annotation { "Feature Type Name" : "Feature", "Feature Type Description" : "" }
export const myFeature = defineFeature(function(context is Context, id is Id, definition is map)
    precondition{}
    {
        {
            var Q0;
            Q0=qCreatedBy(makeId("Right.planeOp"),FACE);
            var sketch = newSketch(context, id + "F0", { "sketchPlane" : qUnion([Q0])});
            skLineSegment(sketch, "E0", {"start": v(-64.38, 0) * mm, "end": v(62.76, 0) * mm, "construction": true});
            skLineSegment(sketch, "E1", {"start": v(-28.58, 0) * mm, "end": v(28.58, 0) * mm});
            skLineSegment(sketch, "E2", {"start": v(-28.58, 0) * mm, "end": v(-28.58, 4.76) * mm});
            skLineSegment(sketch, "E3", {"start": v(0, 21.68) * mm, "end": v(0, -31.61) * mm, "construction": true});
            skPoint(sketch, "E4", {"position": v(0, -63.5) * mm});
            skArc(sketch, "E5", {"start": v(28.58, 4.76) * mm, "mid": v(0, 10.5) * mm, "end": v(-28.58, 4.76) * mm});
            skLineSegment(sketch, "E6", {"start": v(28.58, 0) * mm, "end": v(28.58, 4.76) * mm});
            skSolve(sketch);
        }
        {
            var Q0;
            Q0 = qSketchRegion(id + "F0", true);
            extrude(context, id + "F1", {"entities" : qUnion([Q0]), "endBound" : BoundingType.SYMMETRIC, "depth" : 152.4 * mm, "offsetDistance" : 25.4 * mm});
        }
        {
            var Q0;
            Q0=qCreatedBy(makeId("Right.planeOp"),FACE);
            var sketch = newSketch(context, id + "F2", { "sketchPlane" : qUnion([Q0])});
            skLineSegment(sketch, "E7.bottom", {"start": v(-22.22, 24.41) * mm, "end": v(22.23, 24.41) * mm});
            skLineSegment(sketch, "E7.left", {"start": v(-22.22, 24.41) * mm, "end": v(-22.22, 7) * mm});
            skLineSegment(sketch, "E7.right", {"start": v(22.23, 24.41) * mm, "end": v(22.23, 7) * mm});
            skLineSegment(sketch, "E8", {"start": v(0, 26.13) * mm, "end": v(0, -12.17) * mm, "construction": true});
            skLineSegment(sketch, "E9", {"start": v(-39.48, 0) * mm, "end": v(39.93, 0) * mm, "construction": true});
            skLineSegment(sketch, "E10", {"start": v(-3.17, 21.37) * mm, "end": v(-3.17, -2.67) * mm, "construction": true});
            skLineSegment(sketch, "E11", {"start": v(-6.35, 21.57) * mm, "end": v(-6.35, -2.87) * mm, "construction": true});
            skLineSegment(sketch, "E12", {"start": v(-9.52, 21.78) * mm, "end": v(-9.52, -3.08) * mm, "construction": true});
            skLineSegment(sketch, "E13", {"start": v(-12.7, 21.89) * mm, "end": v(-12.7, -4.22) * mm, "construction": true});
            skLineSegment(sketch, "E14", {"start": v(-15.88, 21.89) * mm, "end": v(-15.88, -4.43) * mm, "construction": true});
            skLineSegment(sketch, "E15", {"start": v(-19.05, 22.3) * mm, "end": v(-19.05, -4.9) * mm, "construction": true});
            skArc(sketch, "E16", {"start": v(-19.58, 5.95) * mm, "mid": v(-20.33, 6.32) * mm, "end": v(-21.17, 6.26) * mm});
            skArc(sketch, "E17", {"start": v(-16.4, 5.95) * mm, "mid": v(-17.46, 6.35) * mm, "end": v(-18.52, 5.95) * mm});
            skArc(sketch, "E18", {"start": v(-13.23, 5.95) * mm, "mid": v(-14.29, 6.35) * mm, "end": v(-15.35, 5.95) * mm});
            skArc(sketch, "E19", {"start": v(-10.05, 5.95) * mm, "mid": v(-11.11, 6.35) * mm, "end": v(-12.17, 5.95) * mm});
            skArc(sketch, "E20", {"start": v(-6.88, 5.95) * mm, "mid": v(-7.94, 6.35) * mm, "end": v(-9, 5.95) * mm});
            skArc(sketch, "E21", {"start": v(-3.7, 5.95) * mm, "mid": v(-4.76, 6.35) * mm, "end": v(-5.82, 5.95) * mm});
            skArc(sketch, "E22", {"start": v(-0.53, 5.95) * mm, "mid": v(-1.59, 6.35) * mm, "end": v(-2.65, 5.95) * mm});
            skArc(sketch, "E23.MirrorCS", {"start": v(19.58, 5.95) * mm, "mid": v(20.33, 6.32) * mm, "end": v(21.17, 6.26) * mm});
            skArc(sketch, "E24.MirrorCS", {"start": v(16.4, 5.95) * mm, "mid": v(17.46, 6.35) * mm, "end": v(18.52, 5.95) * mm});
            skArc(sketch, "E25.MirrorCS", {"start": v(6.88, 5.95) * mm, "mid": v(7.94, 6.35) * mm, "end": v(9, 5.95) * mm});
            skArc(sketch, "E26.MirrorCS", {"start": v(3.7, 5.95) * mm, "mid": v(4.76, 6.35) * mm, "end": v(5.82, 5.95) * mm});
            skArc(sketch, "E27.MirrorCS", {"start": v(10.05, 5.95) * mm, "mid": v(11.11, 6.35) * mm, "end": v(12.17, 5.95) * mm});
            skArc(sketch, "E28.MirrorCS", {"start": v(13.23, 5.95) * mm, "mid": v(14.29, 6.35) * mm, "end": v(15.35, 5.95) * mm});
            skArc(sketch, "E29.MirrorCS", {"start": v(0.53, 5.95) * mm, "mid": v(1.59, 6.35) * mm, "end": v(2.65, 5.95) * mm});
            skArc(sketch, "E30.filletArc", {"start": v(-19.58, 5.95) * mm, "mid": v(-19.05, 5.74) * mm, "end": v(-18.52, 5.95) * mm});
            skArc(sketch, "E31.filletArc", {"start": v(-22.22, 7) * mm, "mid": v(-21.89, 6.36) * mm, "end": v(-21.17, 6.26) * mm});
            skArc(sketch, "E32.filletArc", {"start": v(-16.4, 5.95) * mm, "mid": v(-15.88, 5.74) * mm, "end": v(-15.35, 5.95) * mm});
            skArc(sketch, "E33.filletArc", {"start": v(-13.23, 5.95) * mm, "mid": v(-12.7, 5.74) * mm, "end": v(-12.17, 5.95) * mm});
            skArc(sketch, "E34.filletArc", {"start": v(-10.05, 5.95) * mm, "mid": v(-9.52, 5.74) * mm, "end": v(-9, 5.95) * mm});
            skArc(sketch, "E35.filletArc", {"start": v(-6.88, 5.95) * mm, "mid": v(-6.35, 5.74) * mm, "end": v(-5.82, 5.95) * mm});
            skArc(sketch, "E36.filletArc", {"start": v(-3.7, 5.95) * mm, "mid": v(-3.17, 5.74) * mm, "end": v(-2.65, 5.95) * mm});
            skArc(sketch, "E37.filletArc", {"start": v(-0.53, 5.95) * mm, "mid": v(0, 5.74) * mm, "end": v(0.53, 5.95) * mm});
            skArc(sketch, "E38.filletArc", {"start": v(2.65, 5.95) * mm, "mid": v(3.17, 5.74) * mm, "end": v(3.7, 5.95) * mm});
            skArc(sketch, "E39.filletArc", {"start": v(5.82, 5.95) * mm, "mid": v(6.35, 5.74) * mm, "end": v(6.88, 5.95) * mm});
            skArc(sketch, "E40.filletArc", {"start": v(9, 5.95) * mm, "mid": v(9.52, 5.74) * mm, "end": v(10.05, 5.95) * mm});
            skArc(sketch, "E41.filletArc", {"start": v(12.17, 5.95) * mm, "mid": v(12.7, 5.74) * mm, "end": v(13.23, 5.95) * mm});
            skArc(sketch, "E42.filletArc", {"start": v(15.35, 5.95) * mm, "mid": v(15.88, 5.74) * mm, "end": v(16.4, 5.95) * mm});
            skArc(sketch, "E43.filletArc", {"start": v(18.52, 5.95) * mm, "mid": v(19.05, 5.74) * mm, "end": v(19.58, 5.95) * mm});
            skArc(sketch, "E44.filletArc", {"start": v(21.17, 6.26) * mm, "mid": v(21.89, 6.36) * mm, "end": v(22.23, 7) * mm});
            skSolve(sketch);
        }
        {
            var Q0;
            Q0 = qSketchRegion(id + "F2", true);
            extrude(context, id + "F3", {"entities" : qUnion([Q0]), "operationType" : NewBodyOperationType.REMOVE, "endBound" : BoundingType.SYMMETRIC, "depth" : 139.7 * mm, "offsetDistance" : 25.4 * mm});
        }
        {
            var Q0;
            Q0=qCreatedBy(makeId("Top.planeOp"),FACE);
            var sketch = newSketch(context, id + "F4", { "sketchPlane" : qUnion([Q0])});
            skLineSegment(sketch, "E45", {"start": v(-61.52, 0) * mm, "end": v(67.76, 0) * mm, "construction": true});
            skLineSegment(sketch, "E46", {"start": v(0, 23.15) * mm, "end": v(0, -30.49) * mm, "construction": true});
            skText(sketch, "E47", { "text": "Pappy Bar", "fontName": "RobotoSlab-Bold.ttf"});
            const initialGuessF4  = {"E47": [-0.0635, -0.00927, 1, 0, 0.01857]};
            skSetInitialGuess(sketch, initialGuessF4);
            skSolve(sketch);
        }
        {
            var Q0;
            Q0 = qSketchRegion(id + "F4", true);
            extrude(context, id + "F5", {"entities" : qUnion([Q0]), "operationType" : NewBodyOperationType.ADD, "depth" : 12.7 * mm, "offsetDistance" : 25.4 * mm});
        }
        {
            var Q0;
            Q0=qCreatedBy(makeId("Right.planeOp"),FACE);
            var sketch = newSketch(context, id + "F6", { "sketchPlane" : qUnion([Q0])});
            skLineSegment(sketch, "E48", {"start": v(0, 61.11) * mm, "end": v(0, -83.47) * mm, "construction": true});
            skLineSegment(sketch, "E49", {"start": v(-121.03, 0) * mm, "end": v(89.55, 0) * mm, "construction": true});
            skPoint(sketch, "E50", {"position": v(0, -65.09) * mm});
            skPoint(sketch, "E51", {"position": v(28.58, 3.18) * mm});
            skArc(sketch, "E52", {"start": v(19.05, 6.42) * mm, "mid": v(0, 8.91) * mm, "end": v(-19.05, 6.42) * mm});
            skLineSegment(sketch, "E53.bottom", {"start": v(-19.05, 51.23) * mm, "end": v(19.05, 51.23) * mm});
            skLineSegment(sketch, "E53.left", {"start": v(-19.05, 51.23) * mm, "end": v(-19.05, 6.42) * mm});
            skLineSegment(sketch, "E53.right", {"start": v(19.05, 51.23) * mm, "end": v(19.05, 6.42) * mm});
            skSolve(sketch);
        }
        {
            var Q0;
            Q0 = qSketchRegion(id + "F6", true);
            extrude(context, id + "F7", {"entities" : qUnion([Q0]), "operationType" : NewBodyOperationType.REMOVE, "endBound" : BoundingType.SYMMETRIC, "oppositeDirection" : true, "depth" : 130.17 * mm, "offsetDistance" : 25.4 * mm});
        }
        {
            var Q0;
            Q0=makeQuery(id+"F1.opExtrude","CAP_EDGE",EDGE,{"disambiguationData":[OSD([sQuery(id+"F0.wireOp",EDGE,"E2")])],"isStart":true});
            var Q1;
            Q1=makeQuery(id+"F1.opExtrude","CAP_EDGE",EDGE,{"disambiguationData":[OSD([sQuery(id+"F0.wireOp",EDGE,"E5")])],"isStart":true});
            var Q2;
            Q2=makeQuery(id+"F1.opExtrude","SWEPT_EDGE",EDGE,{"disambiguationData":[OSD([sQuery(id+"F0.wireOp",EDGE,"E2"),sQuery(id+"F0.wireOp",EDGE,"E5")])]});
            var Q3;
            Q3=makeQuery(id+"F1.opExtrude","CAP_EDGE",EDGE,{"disambiguationData":[OSD([sQuery(id+"F0.wireOp",EDGE,"E6")])],"isStart":true});
            var Q4;
            Q4=makeQuery(id+"F1.opExtrude","SWEPT_EDGE",EDGE,{"disambiguationData":[OSD([sQuery(id+"F0.wireOp",EDGE,"E5"),sQuery(id+"F0.wireOp",EDGE,"E6")])]});
            var Q5;
            Q5=makeQuery(id+"F1.opExtrude","CAP_EDGE",EDGE,{"disambiguationData":[OSD([sQuery(id+"F0.wireOp",EDGE,"E6")])],"isStart":false});
            var Q6;
            Q6=makeQuery(id+"F1.opExtrude","CAP_EDGE",EDGE,{"disambiguationData":[OSD([sQuery(id+"F0.wireOp",EDGE,"E5")])],"isStart":false});
            var Q7;
            Q7=makeQuery(id+"F1.opExtrude","CAP_EDGE",EDGE,{"disambiguationData":[OSD([sQuery(id+"F0.wireOp",EDGE,"E2")])],"isStart":false});
            var Q8;
            Q8=makeQuery(id+"F3.boolean.opBoolean","INTERSECT",EDGE,{"derivedFrom":[makeQuery(id+"F1.opExtrude","SWEPT_FACE",FACE,{"disambiguationData":[OSD([sQuery(id+"F0.wireOp",EDGE,"E5")])]}),makeQuery(id+"F3.opExtrude","CAP_FACE",FACE,{"disambiguationData":[OSD([sQuery(id+"F2.wireOp",EDGE,"E7.bottom"),sQuery(id+"F2.wireOp",EDGE,"E7.left"),sQuery(id+"F2.wireOp",EDGE,"E7.right"),sQuery(id+"F2.wireOp",EDGE,"E16"),sQuery(id+"F2.wireOp",EDGE,"E17"),sQuery(id+"F2.wireOp",EDGE,"E18"),sQuery(id+"F2.wireOp",EDGE,"E19"),sQuery(id+"F2.wireOp",EDGE,"E20"),sQuery(id+"F2.wireOp",EDGE,"E21"),sQuery(id+"F2.wireOp",EDGE,"E22"),sQuery(id+"F2.wireOp",EDGE,"E23.MirrorCS"),sQuery(id+"F2.wireOp",EDGE,"E24.MirrorCS"),sQuery(id+"F2.wireOp",EDGE,"E25.MirrorCS"),sQuery(id+"F2.wireOp",EDGE,"E26.MirrorCS"),sQuery(id+"F2.wireOp",EDGE,"E27.MirrorCS"),sQuery(id+"F2.wireOp",EDGE,"E28.MirrorCS"),sQuery(id+"F2.wireOp",EDGE,"E29.MirrorCS"),sQuery(id+"F2.wireOp",EDGE,"E30.filletArc"),sQuery(id+"F2.wireOp",EDGE,"E31.filletArc"),sQuery(id+"F2.wireOp",EDGE,"E32.filletArc"),sQuery(id+"F2.wireOp",EDGE,"E33.filletArc"),sQuery(id+"F2.wireOp",EDGE,"E34.filletArc"),sQuery(id+"F2.wireOp",EDGE,"E35.filletArc"),sQuery(id+"F2.wireOp",EDGE,"E36.filletArc"),sQuery(id+"F2.wireOp",EDGE,"E37.filletArc"),sQuery(id+"F2.wireOp",EDGE,"E38.filletArc"),sQuery(id+"F2.wireOp",EDGE,"E39.filletArc"),sQuery(id+"F2.wireOp",EDGE,"E40.filletArc"),sQuery(id+"F2.wireOp",EDGE,"E41.filletArc"),sQuery(id+"F2.wireOp",EDGE,"E42.filletArc"),sQuery(id+"F2.wireOp",EDGE,"E43.filletArc"),sQuery(id+"F2.wireOp",EDGE,"E44.filletArc")])],"isStart":true})]});
            var Q9;
            Q9=makeQuery(id+"F3.boolean.opBoolean","INTERSECT",EDGE,{"derivedFrom":[makeQuery(id+"F1.opExtrude","SWEPT_FACE",FACE,{"disambiguationData":[OSD([sQuery(id+"F0.wireOp",EDGE,"E5")])]}),makeQuery(id+"F3.opExtrude","CAP_FACE",FACE,{"disambiguationData":[OSD([sQuery(id+"F2.wireOp",EDGE,"E7.bottom"),sQuery(id+"F2.wireOp",EDGE,"E7.left"),sQuery(id+"F2.wireOp",EDGE,"E7.right"),sQuery(id+"F2.wireOp",EDGE,"E16"),sQuery(id+"F2.wireOp",EDGE,"E17"),sQuery(id+"F2.wireOp",EDGE,"E18"),sQuery(id+"F2.wireOp",EDGE,"E19"),sQuery(id+"F2.wireOp",EDGE,"E20"),sQuery(id+"F2.wireOp",EDGE,"E21"),sQuery(id+"F2.wireOp",EDGE,"E22"),sQuery(id+"F2.wireOp",EDGE,"E23.MirrorCS"),sQuery(id+"F2.wireOp",EDGE,"E24.MirrorCS"),sQuery(id+"F2.wireOp",EDGE,"E25.MirrorCS"),sQuery(id+"F2.wireOp",EDGE,"E26.MirrorCS"),sQuery(id+"F2.wireOp",EDGE,"E27.MirrorCS"),sQuery(id+"F2.wireOp",EDGE,"E28.MirrorCS"),sQuery(id+"F2.wireOp",EDGE,"E29.MirrorCS"),sQuery(id+"F2.wireOp",EDGE,"E30.filletArc"),sQuery(id+"F2.wireOp",EDGE,"E31.filletArc"),sQuery(id+"F2.wireOp",EDGE,"E32.filletArc"),sQuery(id+"F2.wireOp",EDGE,"E33.filletArc"),sQuery(id+"F2.wireOp",EDGE,"E34.filletArc"),sQuery(id+"F2.wireOp",EDGE,"E35.filletArc"),sQuery(id+"F2.wireOp",EDGE,"E36.filletArc"),sQuery(id+"F2.wireOp",EDGE,"E37.filletArc"),sQuery(id+"F2.wireOp",EDGE,"E38.filletArc"),sQuery(id+"F2.wireOp",EDGE,"E39.filletArc"),sQuery(id+"F2.wireOp",EDGE,"E40.filletArc"),sQuery(id+"F2.wireOp",EDGE,"E41.filletArc"),sQuery(id+"F2.wireOp",EDGE,"E42.filletArc"),sQuery(id+"F2.wireOp",EDGE,"E43.filletArc"),sQuery(id+"F2.wireOp",EDGE,"E44.filletArc")])],"isStart":false})]});
            var Q10;
            Q10=makeQuery(id+"F3.boolean.opBoolean","INTERSECT",EDGE,{"derivedFrom":[makeQuery(id+"F1.opExtrude","SWEPT_FACE",FACE,{"disambiguationData":[OSD([sQuery(id+"F0.wireOp",EDGE,"E5")])]}),makeQuery(id+"F3.opExtrude","SWEPT_FACE",FACE,{"disambiguationData":[OSD([sQuery(id+"F2.wireOp",EDGE,"E7.right")])]})]});
            var Q11;
            Q11=makeQuery(id+"F3.boolean.opBoolean","INTERSECT",EDGE,{"derivedFrom":[makeQuery(id+"F1.opExtrude","SWEPT_FACE",FACE,{"disambiguationData":[OSD([sQuery(id+"F0.wireOp",EDGE,"E5")])]}),makeQuery(id+"F3.opExtrude","SWEPT_FACE",FACE,{"disambiguationData":[OSD([sQuery(id+"F2.wireOp",EDGE,"E7.left")])]})]});
            fillet(context, id + "F8", {"entities" : qUnion([Q0, Q1, Q2, Q3, Q4, Q5, Q6, Q7, Q8, Q9, Q10, Q11]), "radius" : 2.54 * mm, "tangentPropagation" : true, "allowEdgeOverflow" : false});
        }
    });